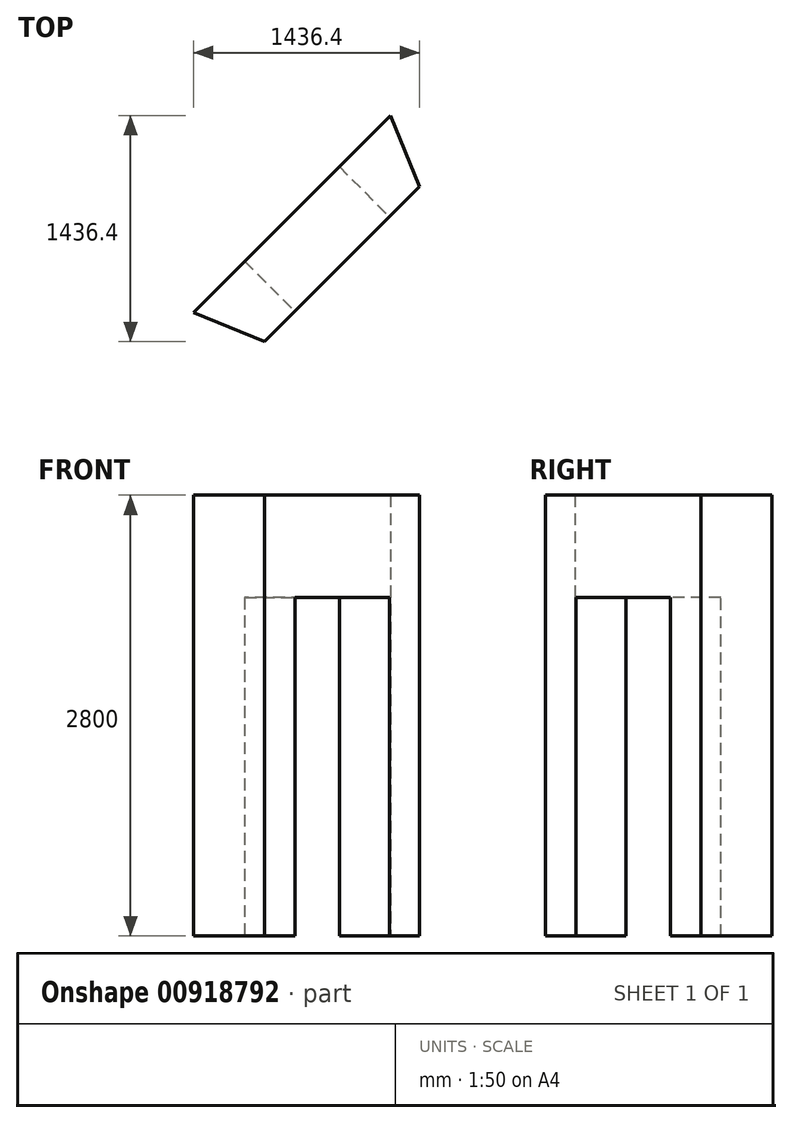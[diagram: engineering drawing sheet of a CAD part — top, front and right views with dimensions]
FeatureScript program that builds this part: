
annotation { "Feature Type Name" : "Feature", "Feature Type Description" : "" }
export const myFeature = defineFeature(function(context is Context, id is Id, definition is map)
    precondition{}
    {
        {
            var Q0;
            Q0=qCreatedBy(makeId("Top.planeOp"),FACE);
            var sketch = newSketch(context, id + "F0", { "sketchPlane" : qUnion([Q0])});
            skLineSegment(sketch, "E0", {"start": v(0, 0) * mm, "end": v(0, 750) * mm, "construction": true});
            skLineSegment(sketch, "E1", {"start": v(0, 750) * mm, "end": v(1250, 2000) * mm, "construction": true});
            skLineSegment(sketch, "E2", {"start": v(1250, 2000) * mm, "end": v(2250, 2000) * mm, "construction": true});
            skLineSegment(sketch, "E3", {"start": v(0, 750) * mm, "end": v(450, 563.6) * mm});
            skLineSegment(sketch, "E4", {"start": v(450, 563.6) * mm, "end": v(1436.4, 1550) * mm});
            skLineSegment(sketch, "E5", {"start": v(1436.4, 1550) * mm, "end": v(1250, 2000) * mm});
            skLineSegment(sketch, "E6", {"start": v(0, 750) * mm, "end": v(1250, 2000) * mm});
            skSolve(sketch);
        }
        {
            var Q0;
            Q0=makeQuery(id+"F0.imprint","IMPRINT",FACE,{"disambiguationData":[TD([[makeQuery(id+"F0.imprint","IMPRINT",EDGE,{"derivedFrom":sQuery(id+"F0.wireOp",EDGE,"E3")}),1.0]])]});
            extrude(context, id + "F1", {"entities" : qUnion([Q0]), "depth" : 2800 * mm, "offsetDistance" : 25 * mm});
        }
        {
            var Q0;
            Q0=makeQuery(id+"F1.opExtrude","SWEPT_FACE",FACE,{"disambiguationData":[OSD([sQuery(id+"F0.wireOp",EDGE,"E4")])]});
            var sketch = newSketch(context, id + "F2", { "sketchPlane" : qUnion([Q0])});
            skLineSegment(sketch, "E7", {"start": v(989.21, 0) * mm, "end": v(989.21, 2150) * mm});
            skLineSegment(sketch, "E8", {"start": v(989.21, 2150) * mm, "end": v(1839.21, 2150) * mm});
            skLineSegment(sketch, "E9", {"start": v(1839.21, 2150) * mm, "end": v(1839.21, 0) * mm});
            skLineSegment(sketch, "E10", {"start": v(989.21, 2150) * mm, "end": v(716.73, 2150) * mm, "construction": true});
            skLineSegment(sketch, "E11", {"start": v(1839.21, 2150) * mm, "end": v(2111.7, 2150) * mm, "construction": true});
            skSolve(sketch);
        }
        {
            var Q0;
            {var subQ0=sQuery(id+"F2.wireOp",EDGE,"E7");Q0=makeQuery(id+"F2.imprint","IMPRINT",FACE,{"disambiguationData":[TD([[makeQuery(id+"F2.imprint","IMPRINT",EDGE,{"derivedFrom":subQ0}),-1.0]])]});}
            extrude(context, id + "F3", {"entities" : qUnion([Q0]), "operationType" : NewBodyOperationType.REMOVE, "endBound" : BoundingType.THROUGH_ALL, "oppositeDirection" : true, "depth" : 25 * mm, "offsetDistance" : 25 * mm});
        }
    });
